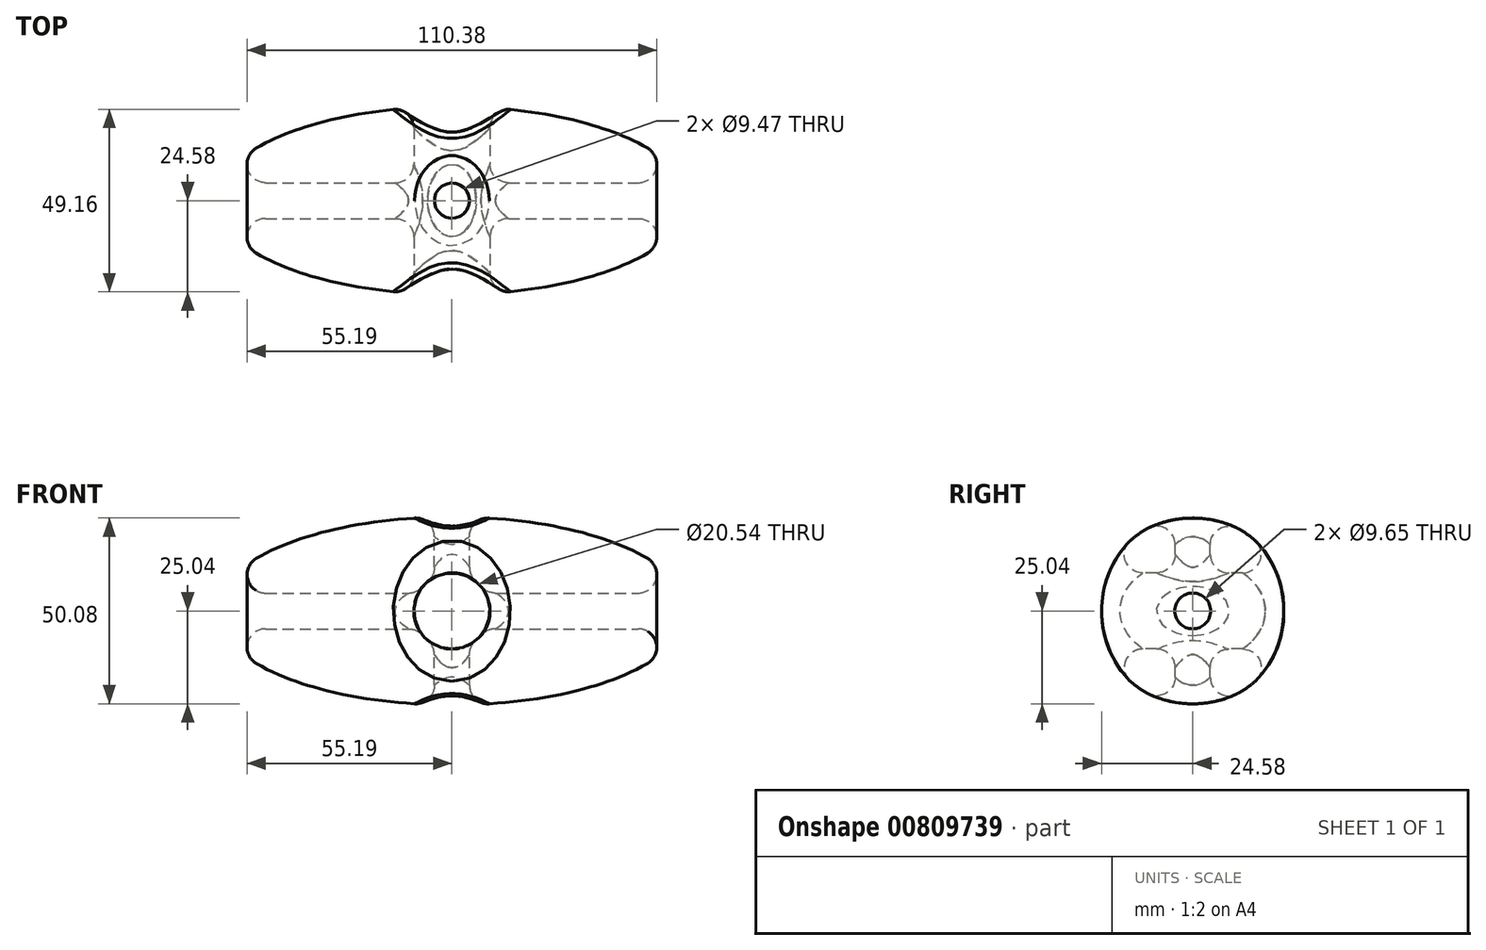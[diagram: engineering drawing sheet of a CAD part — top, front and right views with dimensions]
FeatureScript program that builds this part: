
annotation { "Feature Type Name" : "Feature", "Feature Type Description" : "" }
export const myFeature = defineFeature(function(context is Context, id is Id, definition is map)
    precondition{}
    {
        {
            var Q0;
            Q0=qCreatedBy(makeId("Top.planeOp"),FACE);
            var sketch = newSketch(context, id + "F0", { "sketchPlane" : qUnion([Q0])});
            skEllipticalArc(sketch, "E0", {});
            skLineSegment(sketch, "E1", {"start": v(-63.51, 0) * mm, "end": v(63.51, 0) * mm});
            skPoint(sketch, "E2.orphan", {"position": v(-70.06, 0) * mm});
            const initialGuessF0  = {"E0": [0, 0, 1, 0, 0.0635126605629921, 0.025348355675011588, 0, 3.141592653589793]};
            skSetInitialGuess(sketch, initialGuessF0);
            skSolve(sketch);
        }
        {
            var Q0;
            Q0=qCreatedBy(makeId("Top.planeOp"),FACE);
            var sketch = newSketch(context, id + "F1", { "sketchPlane" : qUnion([Q0])});
            skFitSpline(sketch, "E3.0", {"points": [v(60.96, -1.92) * mm, v(61.2, 0) * mm, v(60.96, 1.92) * mm, v(60.23, 3.88) * mm, v(58.95, 5.91) * mm, v(57.1, 7.97) * mm, v(54.69, 10.02) * mm, v(51.7, 12.02) * mm, v(48.75, 13.6) * mm, v(46.14, 14.82) * mm, v(44.04, 15.7) * mm, v(41.83, 16.54) * mm, v(38.75, 17.6) * mm, v(34.67, 18.8) * mm, v(29.45, 20.05) * mm, v(23.95, 21.09) * mm, v(18.21, 21.9) * mm, v(12.28, 22.5) * mm, v(7.21, 22.8) * mm, v(3.1, 22.93) * mm, v(0, 22.96) * mm, v(-3.1, 22.93) * mm, v(-7.21, 22.8) * mm, v(-12.28, 22.5) * mm, v(-18.21, 21.9) * mm, v(-23.95, 21.09) * mm, v(-29.45, 20.05) * mm, v(-34.67, 18.8) * mm, v(-38.75, 17.6) * mm, v(-41.83, 16.54) * mm, v(-44.04, 15.7) * mm, v(-46.14, 14.82) * mm, v(-48.75, 13.6) * mm, v(-51.7, 12.02) * mm, v(-54.69, 10.02) * mm, v(-57.1, 7.97) * mm, v(-58.95, 5.91) * mm, v(-60.23, 3.88) * mm, v(-60.96, 1.92) * mm, v(-61.2, 0) * mm, v(-60.96, -1.92) * mm, v(-60.23, -3.88) * mm, v(-58.95, -5.91) * mm, v(-57.1, -7.97) * mm, v(-54.69, -10.02) * mm, v(-51.7, -12.02) * mm, v(-48.75, -13.6) * mm, v(-46.14, -14.82) * mm, v(-44.04, -15.7) * mm, v(-41.83, -16.54) * mm, v(-38.75, -17.6) * mm, v(-34.67, -18.8) * mm, v(-29.45, -20.05) * mm, v(-23.95, -21.09) * mm, v(-18.21, -21.9) * mm, v(-12.28, -22.5) * mm, v(-7.21, -22.8) * mm, v(-3.1, -22.93) * mm, v(0, -22.96) * mm, v(3.1, -22.93) * mm, v(7.21, -22.8) * mm, v(12.28, -22.5) * mm, v(18.21, -21.9) * mm, v(23.95, -21.09) * mm, v(29.45, -20.05) * mm, v(34.67, -18.8) * mm, v(38.75, -17.6) * mm, v(41.83, -16.54) * mm, v(44.04, -15.7) * mm, v(46.14, -14.82) * mm, v(48.75, -13.6) * mm, v(51.7, -12.02) * mm, v(54.69, -10.02) * mm, v(57.1, -7.97) * mm, v(58.95, -5.91) * mm, v(60.23, -3.88) * mm, v(60.96, -1.92) * mm, v(61.2, 0) * mm, v(60.96, 1.92) * mm]});
            skLineSegment(sketch, "E4", {"start": v(60.74, 2.4) * mm, "end": v(60.74, 0) * mm});
            skLineSegment(sketch, "E5", {"start": v(-60.74, 2.4) * mm, "end": v(-60.74, 0) * mm});
            skSolve(sketch);
        }
        {
            var Q0;
            Q0 = qSketchRegion(id + "F1", true);
            var Q1;
            Q1=makeQuery(id+"F0.imprint","IMPRINT",FACE,{"disambiguationData":[TD([[makeQuery(id+"F0.imprint","IMPRINT",EDGE,{"derivedFrom":sQuery(id+"F0.wireOp",EDGE,"E0")}),1.0]])]});
            var Q2;
            Q2=sQuery(id+"F0.wireOp",EDGE,"E1");
            revolve(context, id + "F2", {"surfaceOperationType" : NewSurfaceOperationType.NEW, "entities" : qUnion([Q0, Q1]), "axis" : qUnion([Q2]), "revolveType" : RevolveType.FULL});
        }
        {
            var Q0;
            Q0=qCreatedBy(makeId("Front.planeOp"),FACE);
            cPlane(context, id + "F3", {"entities" : qUnion([Q0]), "cplaneType" : CPlaneType.OFFSET, "offset" : 33.4 * mm, "width" : 150 * mm, "height" : 150 * mm});
        }
        {
            var Q0;
            Q0=qCreatedBy(id+"F3.planeOp",FACE);
            var sketch = newSketch(context, id + "F4", { "sketchPlane" : qUnion([Q0])});
            skCircle(sketch, "E6", {"center": v(0, 0) * mm, "radius": 10.27 * mm});
            skSolve(sketch);
        }
        {
            var Q0;
            Q0=makeQuery(id+"F4.imprint","IMPRINT",FACE,{"disambiguationData":[TD([[makeQuery(id+"F4.imprint","IMPRINT",EDGE,{"derivedFrom":sQuery(id+"F4.wireOp",EDGE,"E6")}),1.0]])]});
            extrude(context, id + "F5", {"entities" : qUnion([Q0]), "operationType" : NewBodyOperationType.REMOVE, "oppositeDirection" : true, "depth" : 82 * mm, "offsetDistance" : 25 * mm});
        }
        {
            var Q0;
            Q0=makeQuery(id+"F5.boolean.opBoolean","INTERSECT",EDGE,{"disambiguationData":[OD(0.0)],"derivedFrom":[makeQuery(id+"F2.opRevolve","SWEPT_FACE",FACE,{"disambiguationData":[OSD([sQuery(id+"F0.wireOp",EDGE,"E0")])]}),makeQuery(id+"F5.opExtrude","SWEPT_FACE",FACE,{"disambiguationData":[OSD([sQuery(id+"F4.wireOp",EDGE,"E6")])]})]});
            var Q1;
            Q1=makeQuery(id+"F5.boolean.opBoolean","INTERSECT",EDGE,{"disambiguationData":[OD(1.0)],"derivedFrom":[makeQuery(id+"F2.opRevolve","SWEPT_FACE",FACE,{"disambiguationData":[OSD([sQuery(id+"F0.wireOp",EDGE,"E0")])]}),makeQuery(id+"F5.opExtrude","SWEPT_FACE",FACE,{"disambiguationData":[OSD([sQuery(id+"F4.wireOp",EDGE,"E6")])]})]});
            fillet(context, id + "F6", {"entities" : qUnion([Q0, Q1]), "radius" : 5 * mm, "tangentPropagation" : true, "allowEdgeOverflow" : false});
        }
        {
            var Q0;
            Q0=qCreatedBy(makeId("Right.planeOp"),FACE);
            cPlane(context, id + "F7", {"entities" : qUnion([Q0]), "cplaneType" : CPlaneType.OFFSET, "offset" : 73.4 * mm, "width" : 150 * mm, "height" : 150 * mm});
        }
        {
            var Q0;
            Q0=qCreatedBy(id+"F7.planeOp",FACE);
            var sketch = newSketch(context, id + "F8", { "sketchPlane" : qUnion([Q0])});
            skCircle(sketch, "E7", {"center": v(0, 0) * mm, "radius": 4.82 * mm});
            skSolve(sketch);
        }
        {
            var Q0;
            Q0=makeQuery(id+"F8.imprint","IMPRINT",FACE,{"disambiguationData":[TD([[makeQuery(id+"F8.imprint","IMPRINT",EDGE,{"derivedFrom":sQuery(id+"F8.wireOp",EDGE,"E7")}),1.0]])]});
            extrude(context, id + "F9", {"entities" : qUnion([Q0]), "operationType" : NewBodyOperationType.REMOVE, "oppositeDirection" : true, "depth" : 200 * mm, "offsetDistance" : 25 * mm});
        }
        {
            var Q0;
            Q0=makeQuery(id+"F9.boolean.opBoolean","INTERSECT",EDGE,{"disambiguationData":[OD(0.0)],"derivedFrom":[makeQuery(id+"F2.opRevolve","SWEPT_FACE",FACE,{"disambiguationData":[OSD([sQuery(id+"F0.wireOp",EDGE,"E0")])]}),makeQuery(id+"F9.opExtrude","SWEPT_FACE",FACE,{"disambiguationData":[OSD([sQuery(id+"F8.wireOp",EDGE,"E7")])]})]});
            var Q1;
            Q1=makeQuery(id+"F9.boolean.opBoolean","INTERSECT",EDGE,{"disambiguationData":[OD(1.0)],"derivedFrom":[makeQuery(id+"F2.opRevolve","SWEPT_FACE",FACE,{"disambiguationData":[OSD([sQuery(id+"F0.wireOp",EDGE,"E0")])]}),makeQuery(id+"F9.opExtrude","SWEPT_FACE",FACE,{"disambiguationData":[OSD([sQuery(id+"F8.wireOp",EDGE,"E7")])]})]});
            var Q2;
            Q2=makeQuery(id+"F9.boolean.opBoolean","INTERSECT",EDGE,{"disambiguationData":[OD(1.0)],"derivedFrom":[makeQuery(id+"F5.boolean.opBoolean","COPY",FACE,{"derivedFrom":makeQuery(id+"F5.opExtrude","SWEPT_FACE",FACE,{"disambiguationData":[OSD([sQuery(id+"F4.wireOp",EDGE,"E6")])]})}),makeQuery(id+"F9.opExtrude","SWEPT_FACE",FACE,{"disambiguationData":[OSD([sQuery(id+"F8.wireOp",EDGE,"E7")])]})]});
            var Q3;
            Q3=makeQuery(id+"F9.boolean.opBoolean","INTERSECT",EDGE,{"disambiguationData":[OD(0.0)],"derivedFrom":[makeQuery(id+"F5.boolean.opBoolean","COPY",FACE,{"derivedFrom":makeQuery(id+"F5.opExtrude","SWEPT_FACE",FACE,{"disambiguationData":[OSD([sQuery(id+"F4.wireOp",EDGE,"E6")])]})}),makeQuery(id+"F9.opExtrude","SWEPT_FACE",FACE,{"disambiguationData":[OSD([sQuery(id+"F8.wireOp",EDGE,"E7")])]})]});
            fillet(context, id + "F10", {"entities" : qUnion([Q0, Q1, Q2, Q3]), "radius" : 5 * mm, "tangentPropagation" : true, "allowEdgeOverflow" : false});
        }
        {
            var Q0;
            Q0=qCreatedBy(makeId("Top.planeOp"),FACE);
            cPlane(context, id + "F11", {"entities" : qUnion([Q0]), "cplaneType" : CPlaneType.OFFSET, "offset" : 30 * mm, "width" : 150 * mm, "height" : 150 * mm});
        }
        {
            var Q0;
            Q0=qCreatedBy(id+"F11.planeOp",FACE);
            var sketch = newSketch(context, id + "F12", { "sketchPlane" : qUnion([Q0])});
            skCircle(sketch, "E8", {"center": v(0, 0) * mm, "radius": 4.73 * mm});
            skSolve(sketch);
        }
        {
            var Q0;
            Q0=makeQuery(id+"F12.imprint","IMPRINT",FACE,{"disambiguationData":[TD([[makeQuery(id+"F12.imprint","IMPRINT",EDGE,{"derivedFrom":sQuery(id+"F12.wireOp",EDGE,"E8")}),1.0]])]});
            extrude(context, id + "F13", {"entities" : qUnion([Q0]), "operationType" : NewBodyOperationType.REMOVE, "oppositeDirection" : true, "depth" : 60.4 * mm, "offsetDistance" : 25 * mm});
        }
        {
            var Q0;
            Q0=makeQuery(id+"F13.boolean.opBoolean","INTERSECT",EDGE,{"disambiguationData":[OD(1.0)],"derivedFrom":[makeQuery(id+"F2.opRevolve","SWEPT_FACE",FACE,{"disambiguationData":[OSD([sQuery(id+"F0.wireOp",EDGE,"E0")])]}),makeQuery(id+"F13.opExtrude","SWEPT_FACE",FACE,{"disambiguationData":[OSD([sQuery(id+"F12.wireOp",EDGE,"E8")])]})]});
            var Q1;
            Q1=makeQuery(id+"F13.boolean.opBoolean","INTERSECT",EDGE,{"disambiguationData":[OD(0.0)],"derivedFrom":[makeQuery(id+"F2.opRevolve","SWEPT_FACE",FACE,{"disambiguationData":[OSD([sQuery(id+"F0.wireOp",EDGE,"E0")])]}),makeQuery(id+"F13.opExtrude","SWEPT_FACE",FACE,{"disambiguationData":[OSD([sQuery(id+"F12.wireOp",EDGE,"E8")])]})]});
            var Q2;
            Q2=makeQuery(id+"F13.boolean.opBoolean","INTERSECT",EDGE,{"disambiguationData":[OD(0.0)],"derivedFrom":[makeQuery(id+"F5.boolean.opBoolean","COPY",FACE,{"derivedFrom":makeQuery(id+"F5.opExtrude","SWEPT_FACE",FACE,{"disambiguationData":[OSD([sQuery(id+"F4.wireOp",EDGE,"E6")])]})}),makeQuery(id+"F13.opExtrude","SWEPT_FACE",FACE,{"disambiguationData":[OSD([sQuery(id+"F12.wireOp",EDGE,"E8")])]})]});
            var Q3;
            Q3=makeQuery(id+"F13.boolean.opBoolean","INTERSECT",EDGE,{"disambiguationData":[OD(1.0)],"derivedFrom":[makeQuery(id+"F5.boolean.opBoolean","COPY",FACE,{"derivedFrom":makeQuery(id+"F5.opExtrude","SWEPT_FACE",FACE,{"disambiguationData":[OSD([sQuery(id+"F4.wireOp",EDGE,"E6")])]})}),makeQuery(id+"F13.opExtrude","SWEPT_FACE",FACE,{"disambiguationData":[OSD([sQuery(id+"F12.wireOp",EDGE,"E8")])]})]});
            fillet(context, id + "F14", {"entities" : qUnion([Q0, Q1, Q2, Q3]), "radius" : 5 * mm, "tangentPropagation" : true, "allowEdgeOverflow" : false});
        }
    });
